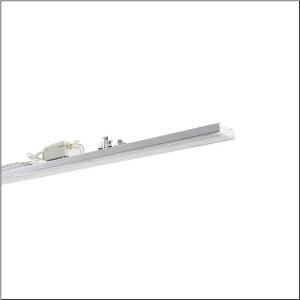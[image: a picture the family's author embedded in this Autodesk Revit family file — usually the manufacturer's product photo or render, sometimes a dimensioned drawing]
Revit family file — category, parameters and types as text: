
# Revit family: licross_r__21_recessed_ho_52tl11dn4axs_508c
name_source: partatom
category: Lighting Fixtures
units: mm (PartAtom-declared; Revit-internal decimal feet)

## family parameters
Cut with Voids When Loaded = No
Host = Face
Light Source = No
Part Type = Normal
Room Calculation Point = No
Round Connector Dimension = Use Diameter
Shared = No

## types (1)
- --- (1 x LED, 10000 lm, 54.7 W, 4000K)
    Apparent Load = 55 VA
    CIE Flux Codes = 87 95 99 100 100
    Color Rendering = 80
    Color Temperature = 4000K
    Default Elevation = 1800 mm
    Description = Licross® 21 Recessed HO, luminaire insert, of sheet steel, galvanised, coil coated, white, length: 1.500mm, width: 66mm, height: 67mm, LED rated luminous flux: 10.000lm, light colour: 840, control gear: DALI 2, with plug, 5-pole, with phase selection, mains connection: 220..240V, AC, 50/60Hz, rated input power: 55W, halogen-free wiring, primary light control with lens, of plastic, primary optical cover: cover, of PMMA, light emission: direct distribution, primary light characteristic: symmetric, protection rating (complete): IP40, insulation class (complete): insulation class I (protective earthing), certification: CE, ENEC, VDE, UKCA, protection symbol: D if used in an environment without relevant dust loads with corresponding accessories, impact resistance: IK06, permissible ambient temperature for indoor applications: -25..+40°C, corresponds to IFS (International Featured Standards) requirements for safety and quality in the food industry, reducing of maximum allowable ambient temperature of 5°C with ceiling mounting, LABS conformity tested according to VDMA 24364:2018-05, packaging unit: 1 piece
    Height = 58 mm
    Lamp = 1 x LED
    Lamp Light Flux = 10000 lm
    Lamp Power = 54.7 W
    Lamp count = 1
    Length = 1500 mm
    Luminous efficacy = 183 lm/W
    Manufacturer = Siteco
    ModVariant = No
    Model = 52TL11DN4AXS
    Mounting Place = Ceiling
    Mounting Type = Pendant
    Number of Poles = 1
    OnlyDefault = Yes
    Power Factor = 1
    Product Name = Licross® 21 Recessed HO
    Product group = luminaire insert
    ProductGroupID = 901
    Protection Class = Protection class I
    Protection Degree = IP 40
    RLX_Detail_Level = 1
    RLX_Emergency_Light_Flux = 0 lm
    RLX_Emergency_Type = 0
    RLX_Emergency_Type_DB = No
    RlxData = <blob elided: 24309 chars, md5=2d28f94d>
    Socket = socket
    Standby Power = 0 W
    System Light Flux = 10000 lm
    System Power = 55 W
    Type Comments = factory setting: luminous flux: 100 % | dim-lin: 254 | 313 mA
    Type Image = l_1296930.jpg
    URL = http://relux.com
    VarID = @adj_058865
    Voltage = 0 V
    Weight = 0.00 kg
    Width = 66 mm

## geometry (parser evidence)
native form markers: Blend x4, Sweep x10
no freeform markers — native parametric forms only
